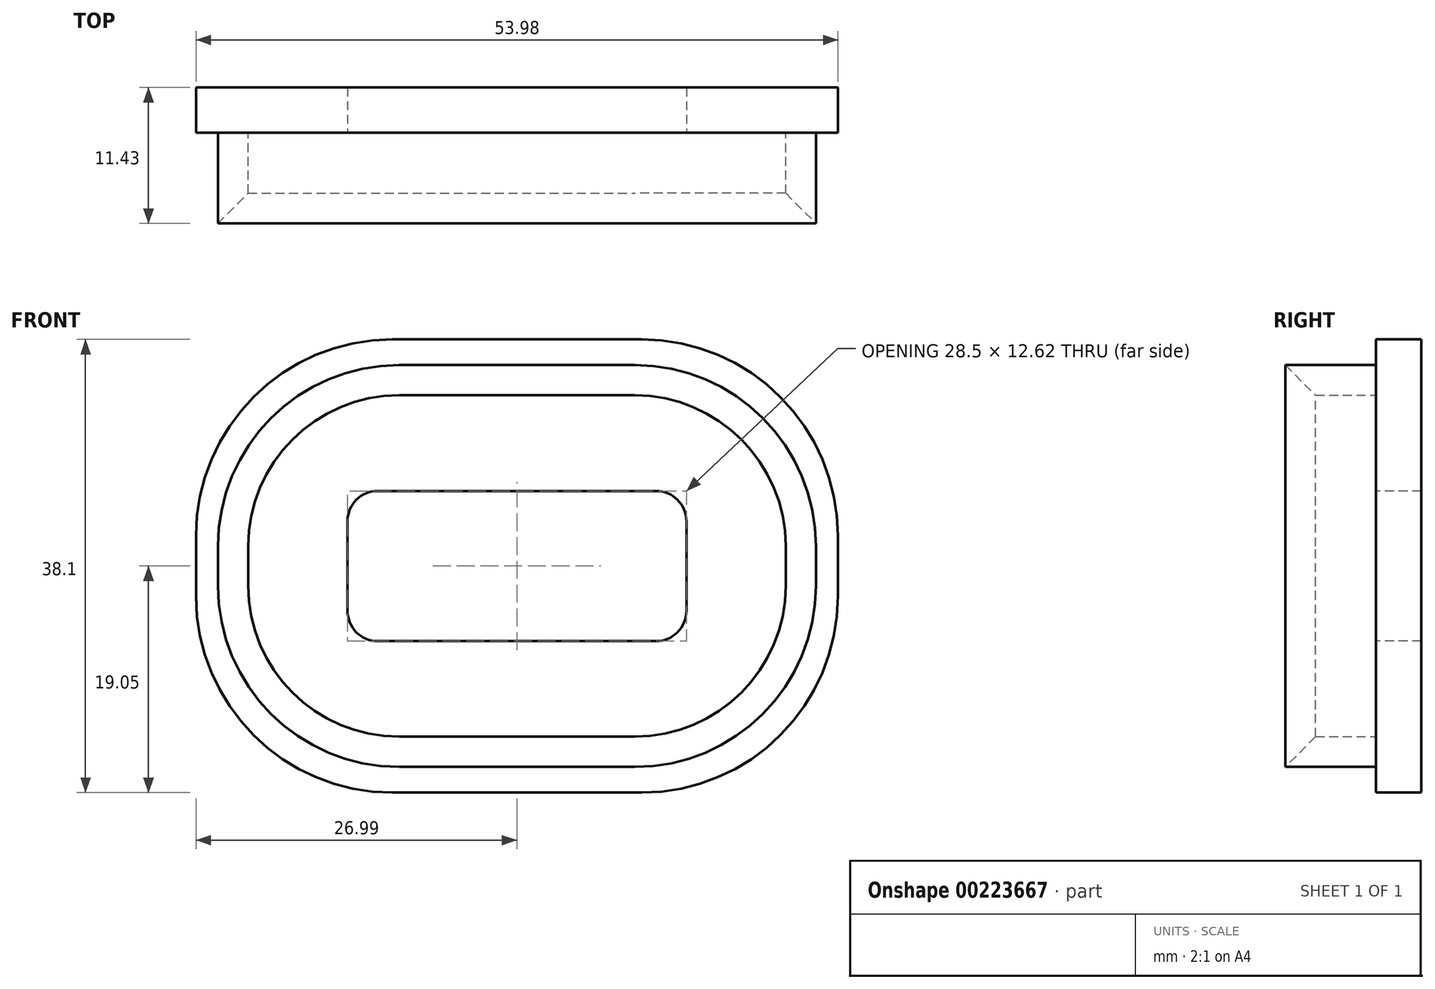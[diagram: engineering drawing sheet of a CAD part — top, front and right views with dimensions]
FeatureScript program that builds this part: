
annotation { "Feature Type Name" : "Feature", "Feature Type Description" : "" }
export const myFeature = defineFeature(function(context is Context, id is Id, definition is map)
    precondition{}
    {
        {
            var Q0;
            Q0=qCreatedBy(makeId("Front.planeOp"),FACE);
            var sketch = newSketch(context, id + "F0", { "sketchPlane" : qUnion([Q0])});
            skLineSegment(sketch, "E0.bottom", {"start": v(-10.48, -19.05) * mm, "end": v(10.48, -19.05) * mm});
            skLineSegment(sketch, "E0.top", {"start": v(-10.48, 19.05) * mm, "end": v(10.48, 19.05) * mm});
            skLineSegment(sketch, "E0.left", {"start": v(-26.99, -2.54) * mm, "end": v(-26.99, 2.54) * mm});
            skLineSegment(sketch, "E0.right", {"start": v(26.99, -2.54) * mm, "end": v(26.99, 2.54) * mm});
            skPoint(sketch, "E0.middle", {"position": v(0, 0) * mm});
            skPoint(sketch, "E1.visualSharp", {"position": v(26.99, 19.05) * mm});
            skArc(sketch, "E1.filletArc", {"start": v(26.99, 2.54) * mm, "mid": v(22.15, 14.21) * mm, "end": v(10.48, 19.05) * mm});
            skPoint(sketch, "E2.visualSharp", {"position": v(-26.99, 19.05) * mm});
            skArc(sketch, "E2.filletArc", {"start": v(-10.48, 19.05) * mm, "mid": v(-22.15, 14.21) * mm, "end": v(-26.99, 2.54) * mm});
            skPoint(sketch, "E3.visualSharp", {"position": v(-26.99, -19.05) * mm});
            skArc(sketch, "E3.filletArc", {"start": v(-26.99, -2.54) * mm, "mid": v(-22.15, -14.21) * mm, "end": v(-10.48, -19.05) * mm});
            skPoint(sketch, "E4.visualSharp", {"position": v(26.99, -19.05) * mm});
            skArc(sketch, "E4.filletArc", {"start": v(10.48, -19.05) * mm, "mid": v(22.15, -14.21) * mm, "end": v(26.99, -2.54) * mm});
            skSolve(sketch);
        }
        {
            var Q0;
            Q0 = qSketchRegion(id + "F0", true);
            extrude(context, id + "F1", {"entities" : qUnion([Q0]), "depth" : 3.8 * mm});
        }
        {
            var Q0;
            Q0=makeQuery(id+"F1.opExtrude","CAP_FACE",FACE,{"disambiguationData":[OSD([sQuery(id+"F0.wireOp",EDGE,"E0.bottom"),sQuery(id+"F0.wireOp",EDGE,"E0.top"),sQuery(id+"F0.wireOp",EDGE,"E0.left"),sQuery(id+"F0.wireOp",EDGE,"E0.right")])],"isStart":false});
            var sketch = newSketch(context, id + "F2", { "sketchPlane" : qUnion([Q0])});
            skLineSegment(sketch, "E5.bottom", {"start": v(-9.9, -14.35) * mm, "end": v(9.9, -14.35) * mm});
            skLineSegment(sketch, "E5.top", {"start": v(-9.9, 14.35) * mm, "end": v(9.9, 14.35) * mm});
            skLineSegment(sketch, "E5.left", {"start": v(-22.6, -1.65) * mm, "end": v(-22.6, 1.65) * mm});
            skLineSegment(sketch, "E5.right", {"start": v(22.6, -1.65) * mm, "end": v(22.6, 1.65) * mm});
            skPoint(sketch, "E5.middle", {"position": v(0, 0) * mm});
            skPoint(sketch, "E6.visualSharp", {"position": v(-22.6, 14.35) * mm});
            skArc(sketch, "E6.filletArc", {"start": v(-9.9, 14.35) * mm, "mid": v(-18.89, 10.63) * mm, "end": v(-22.6, 1.65) * mm});
            skPoint(sketch, "E7.visualSharp", {"position": v(22.6, 14.35) * mm});
            skArc(sketch, "E7.filletArc", {"start": v(22.6, 1.65) * mm, "mid": v(18.89, 10.63) * mm, "end": v(9.9, 14.35) * mm});
            skPoint(sketch, "E8.visualSharp", {"position": v(22.6, -14.35) * mm});
            skArc(sketch, "E8.filletArc", {"start": v(9.9, -14.35) * mm, "mid": v(18.89, -10.63) * mm, "end": v(22.6, -1.65) * mm});
            skPoint(sketch, "E9.visualSharp", {"position": v(-22.6, -14.35) * mm});
            skArc(sketch, "E9.filletArc", {"start": v(-22.6, -1.65) * mm, "mid": v(-18.89, -10.63) * mm, "end": v(-9.9, -14.35) * mm});
            skLineSegment(sketch, "E10.0", {"start": v(-9.9, 16.9) * mm, "end": v(9.9, 16.9) * mm});
            skArc(sketch, "E10.1", {"start": v(-9.9, 16.9) * mm, "mid": v(-20.68, 12.43) * mm, "end": v(-25.15, 1.65) * mm});
            skArc(sketch, "E11.0", {"start": v(25.15, 1.65) * mm, "mid": v(20.68, 12.43) * mm, "end": v(9.9, 16.9) * mm});
            skLineSegment(sketch, "E11.1", {"start": v(25.15, -1.65) * mm, "end": v(25.15, 1.65) * mm});
            skLineSegment(sketch, "E11.2", {"start": v(-25.15, -1.65) * mm, "end": v(-25.15, 1.65) * mm});
            skArc(sketch, "E11.3", {"start": v(-25.15, -1.65) * mm, "mid": v(-20.68, -12.43) * mm, "end": v(-9.9, -16.9) * mm});
            skLineSegment(sketch, "E11.4", {"start": v(-9.9, -16.9) * mm, "end": v(9.9, -16.9) * mm});
            skArc(sketch, "E11.5", {"start": v(9.9, -16.9) * mm, "mid": v(20.68, -12.43) * mm, "end": v(25.15, -1.65) * mm});
            skSolve(sketch);
        }
        {
            var Q0;
            Q0 = qSketchRegion(id + "F2", true);
            extrude(context, id + "F3", {"entities" : qUnion([Q0]), "operationType" : NewBodyOperationType.ADD, "depth" : 7.62 * mm});
        }
        {
            var Q0;
            Q0=makeQuery(id+"F3.boolean.opBoolean","SPLIT",FACE,{"disambiguationData":[TD([makeQuery(id+"F3.opExtrude","SWEPT_FACE",FACE,{"disambiguationData":[OSD([sQuery(id+"F2.wireOp",EDGE,"E5.bottom")])]})])],"derivedFrom":makeQuery(id+"F1.opExtrude","CAP_FACE",FACE,{"disambiguationData":[OSD([sQuery(id+"F0.wireOp",EDGE,"E0.bottom"),sQuery(id+"F0.wireOp",EDGE,"E0.top"),sQuery(id+"F0.wireOp",EDGE,"E0.left"),sQuery(id+"F0.wireOp",EDGE,"E0.right")])],"isStart":false})});
            var sketch = newSketch(context, id + "F4", { "sketchPlane" : qUnion([Q0])});
            skLineSegment(sketch, "E12.bottom", {"start": v(-11.7, -6.31) * mm, "end": v(11.7, -6.31) * mm});
            skLineSegment(sketch, "E12.top", {"start": v(-11.7, 6.31) * mm, "end": v(11.7, 6.31) * mm});
            skLineSegment(sketch, "E12.left", {"start": v(-14.25, -3.77) * mm, "end": v(-14.25, 3.77) * mm});
            skLineSegment(sketch, "E12.right", {"start": v(14.25, -3.77) * mm, "end": v(14.25, 3.77) * mm});
            skPoint(sketch, "E12.middle", {"position": v(0, 0) * mm});
            skPoint(sketch, "E13.visualSharp", {"position": v(-14.25, 6.31) * mm});
            skArc(sketch, "E13.filletArc", {"start": v(-11.7, 6.31) * mm, "mid": v(-13.5, 5.57) * mm, "end": v(-14.25, 3.77) * mm});
            skPoint(sketch, "E14.visualSharp", {"position": v(14.25, 6.31) * mm});
            skArc(sketch, "E14.filletArc", {"start": v(14.25, 3.77) * mm, "mid": v(13.5, 5.57) * mm, "end": v(11.7, 6.31) * mm});
            skPoint(sketch, "E15.visualSharp", {"position": v(14.25, -6.31) * mm});
            skArc(sketch, "E15.filletArc", {"start": v(11.7, -6.31) * mm, "mid": v(13.5, -5.57) * mm, "end": v(14.25, -3.77) * mm});
            skPoint(sketch, "E16.visualSharp", {"position": v(-14.25, -6.31) * mm});
            skArc(sketch, "E16.filletArc", {"start": v(-14.25, -3.77) * mm, "mid": v(-13.5, -5.57) * mm, "end": v(-11.7, -6.31) * mm});
            skSolve(sketch);
        }
        {
            var Q0;
            Q0 = qSketchRegion(id + "F4", true);
            extrude(context, id + "F5", {"entities" : qUnion([Q0]), "operationType" : NewBodyOperationType.REMOVE, "endBound" : BoundingType.THROUGH_ALL, "oppositeDirection" : true, "depth" : 25.4 * mm});
        }
        {
            var Q0;
            Q0=makeQuery(id+"F3.opExtrude","CAP_EDGE",EDGE,{"disambiguationData":[OSD([sQuery(id+"F2.wireOp",EDGE,"E6.filletArc")])],"isStart":false});
            var Q1;
            Q1=makeQuery(id+"F3.opExtrude","CAP_EDGE",EDGE,{"disambiguationData":[OSD([sQuery(id+"F2.wireOp",EDGE,"E5.top")])],"isStart":false});
            var Q2;
            Q2=makeQuery(id+"F3.opExtrude","CAP_EDGE",EDGE,{"disambiguationData":[OSD([sQuery(id+"F2.wireOp",EDGE,"E7.filletArc")])],"isStart":false});
            var Q3;
            Q3=makeQuery(id+"F3.opExtrude","CAP_EDGE",EDGE,{"disambiguationData":[OSD([sQuery(id+"F2.wireOp",EDGE,"E8.filletArc")])],"isStart":false});
            var Q4;
            Q4=makeQuery(id+"F3.opExtrude","CAP_EDGE",EDGE,{"disambiguationData":[OSD([sQuery(id+"F2.wireOp",EDGE,"E9.filletArc")])],"isStart":false});
            var Q5;
            Q5=makeQuery(id+"F3.opExtrude","CAP_EDGE",EDGE,{"disambiguationData":[OSD([sQuery(id+"F2.wireOp",EDGE,"E5.bottom")])],"isStart":false});
            var Q6;
            Q6=makeQuery(id+"F3.opExtrude","CAP_EDGE",EDGE,{"disambiguationData":[OSD([sQuery(id+"F2.wireOp",EDGE,"E5.right")])],"isStart":false});
            var Q7;
            Q7=makeQuery(id+"F3.opExtrude","CAP_EDGE",EDGE,{"disambiguationData":[OSD([sQuery(id+"F2.wireOp",EDGE,"E5.left")])],"isStart":false});
            chamfer(context, id + "F6", {"entities" : qUnion([Q0, Q1, Q2, Q3, Q4, Q5, Q6, Q7]), "width" : 2.54 * mm, "tangentPropagation" : true});
        }
    });
